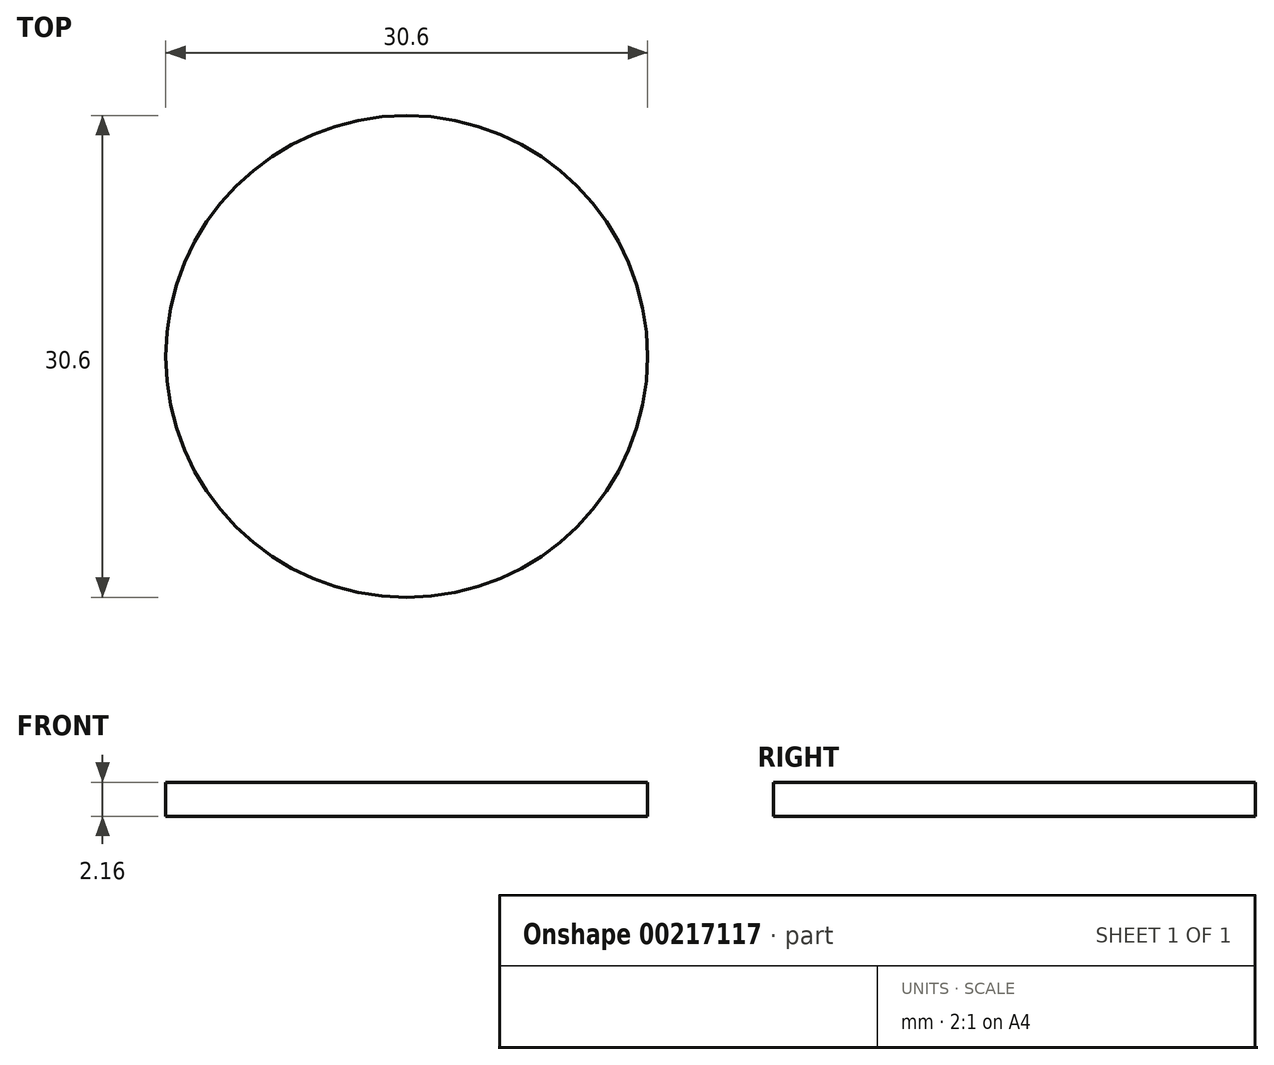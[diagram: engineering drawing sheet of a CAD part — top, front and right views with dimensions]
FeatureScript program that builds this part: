
annotation { "Feature Type Name" : "Feature", "Feature Type Description" : "" }
export const myFeature = defineFeature(function(context is Context, id is Id, definition is map)
    precondition{}
    {
        {
            var Q0;
            Q0=qCreatedBy(makeId("Top.planeOp"),FACE);
            var sketch = newSketch(context, id + "F0", { "sketchPlane" : qUnion([Q0])});
            skCircle(sketch, "E0", {"center": v(0, 0) * mm, "radius": 15.3 * mm});
            skSolve(sketch);
        }
        {
            var Q0;
            Q0 = qSketchRegion(id + "F0", true);
            extrude(context, id + "F1", {"entities" : qUnion([Q0]), "endBound" : BoundingType.SYMMETRIC, "depth" : 2.15 * mm});
        }
    });
